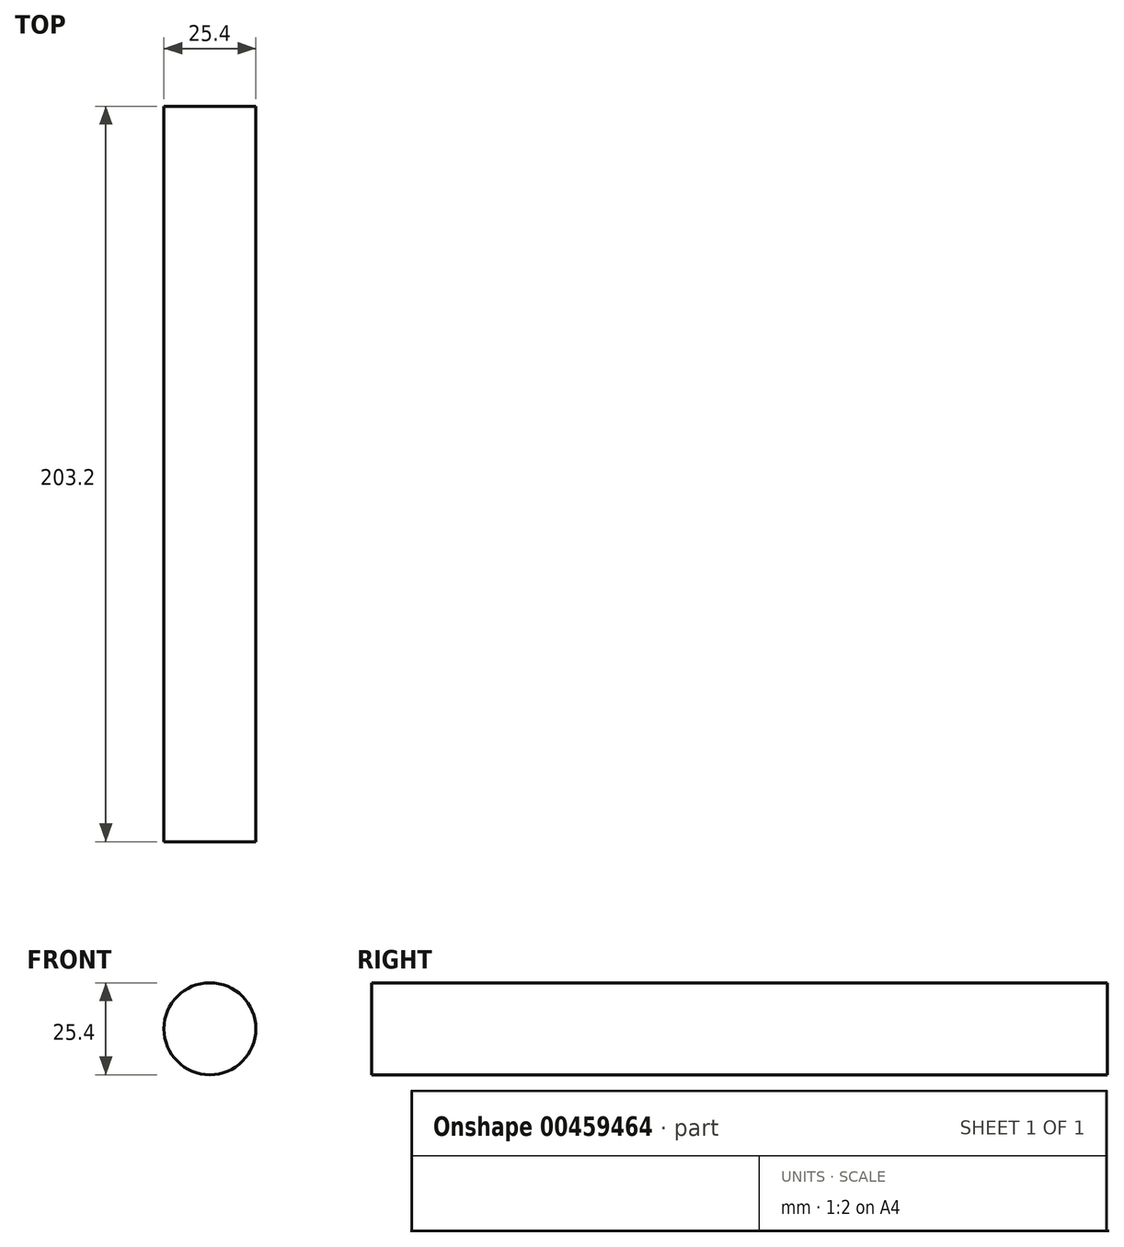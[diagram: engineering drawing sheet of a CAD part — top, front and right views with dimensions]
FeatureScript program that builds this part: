
annotation { "Feature Type Name" : "Feature", "Feature Type Description" : "" }
export const myFeature = defineFeature(function(context is Context, id is Id, definition is map)
    precondition{}
    {
        {
            var Q0;
            Q0=qCreatedBy(makeId("Front.planeOp"),FACE);
            var sketch = newSketch(context, id + "F0", { "sketchPlane" : qUnion([Q0])});
            skCircle(sketch, "E0", {"center": v(0, 0) * mm, "radius": 12.7 * mm});
            skSolve(sketch);
        }
        {
            var Q0;
            Q0=qSketchRegion(id+"F0",true);
            extrude(context, id + "F1", {"entities" : qUnion([Q0]), "depth" : 203.2 * mm});
        }
    });
